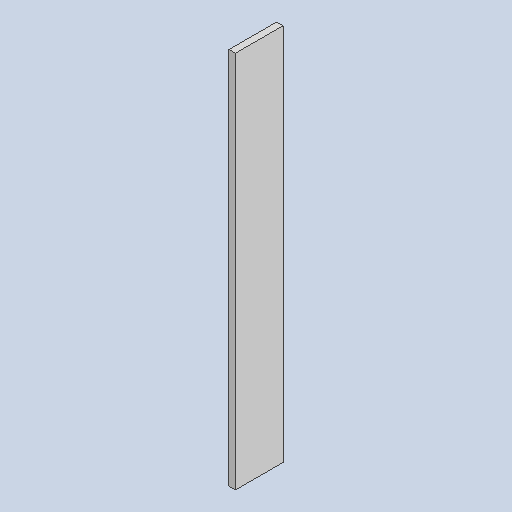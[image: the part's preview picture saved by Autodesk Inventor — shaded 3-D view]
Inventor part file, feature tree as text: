
AUTODESK INVENTOR PART (.ipt)
format: ipt  version: 2025 (Build 290162010, 162A)  size: 88,576 bytes
history: native  units: mm
features: extrude x1, sketch x1
ambient origin geometry x8: Origin, YZ Plane, XZ Plane, XY Plane, X Axis, Y Axis, Z Axis, Center Point
bodies: Solid1 (feature_tree)
feature tree (2):
  extrude  "Extrusion1"  Depth=74.0mm
  sketch  "Sketch1"  dims[d0=513.0mm d1=260.0mm d2=635.0mm d6=5.0mm d7=74.0mm d8=0.0mm]
